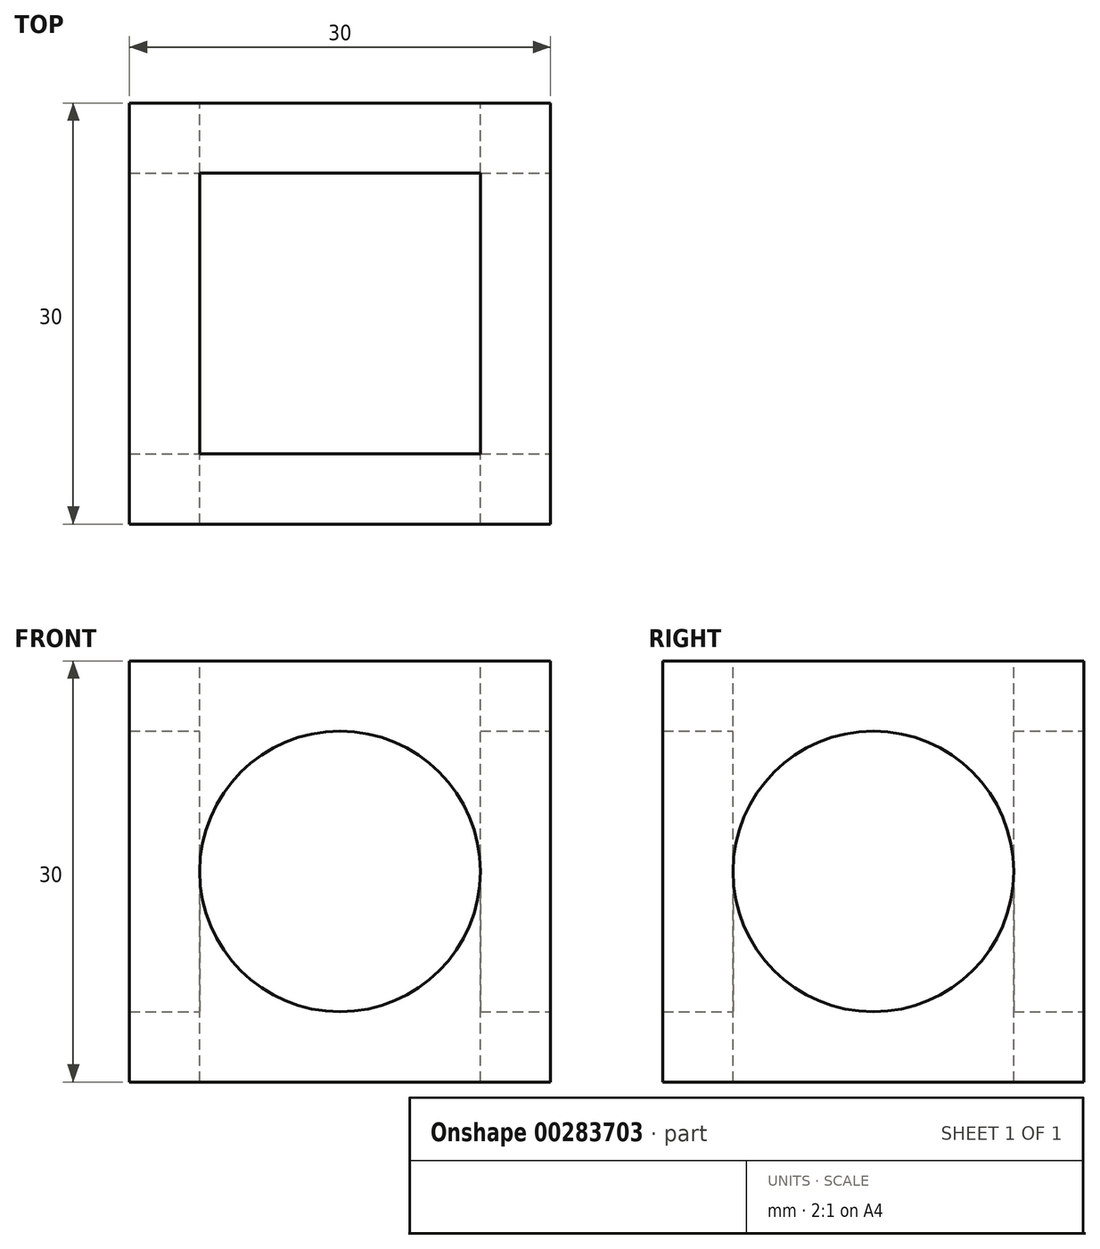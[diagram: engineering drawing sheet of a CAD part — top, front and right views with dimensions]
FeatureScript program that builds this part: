
annotation { "Feature Type Name" : "Feature", "Feature Type Description" : "" }
export const myFeature = defineFeature(function(context is Context, id is Id, definition is map)
    precondition{}
    {
        {
            var Q0;
            Q0=qCreatedBy(makeId("Top.planeOp"),FACE);
            var sketch = newSketch(context, id + "F0", { "sketchPlane" : qUnion([Q0])});
            skLineSegment(sketch, "E0.bottom", {"start": v(15, 15) * mm, "end": v(-15, 15) * mm});
            skLineSegment(sketch, "E0.top", {"start": v(15, -15) * mm, "end": v(-15, -15) * mm});
            skLineSegment(sketch, "E0.left", {"start": v(15, 15) * mm, "end": v(15, -15) * mm});
            skLineSegment(sketch, "E0.right", {"start": v(-15, 15) * mm, "end": v(-15, -15) * mm});
            skPoint(sketch, "E0.middle", {"position": v(0, 0) * mm});
            skSolve(sketch);
        }
        {
            var Q0;
            Q0 = qSketchRegion(id + "F0", true);
            extrude(context, id + "F1", {"entities" : qUnion([Q0]), "endBound" : BoundingType.SYMMETRIC, "depth" : 30 * mm});
        }
        {
            var Q0;
            Q0=makeQuery(id+"F1.opExtrude","CAP_FACE",FACE,{"disambiguationData":[OSD([sQuery(id+"F0.wireOp",EDGE,"E0.bottom"),sQuery(id+"F0.wireOp",EDGE,"E0.top"),sQuery(id+"F0.wireOp",EDGE,"E0.left"),sQuery(id+"F0.wireOp",EDGE,"E0.right")])],"isStart":false});
            var sketch = newSketch(context, id + "F2", { "sketchPlane" : qUnion([Q0])});
            skLineSegment(sketch, "E1.bottom", {"start": v(10, 10) * mm, "end": v(-10, 10) * mm});
            skLineSegment(sketch, "E1.top", {"start": v(10, -10) * mm, "end": v(-10, -10) * mm});
            skLineSegment(sketch, "E1.left", {"start": v(10, 10) * mm, "end": v(10, -10) * mm});
            skLineSegment(sketch, "E1.right", {"start": v(-10, 10) * mm, "end": v(-10, -10) * mm});
            skPoint(sketch, "E1.middle", {"position": v(0, 0) * mm});
            skSolve(sketch);
        }
        {
            var Q0;
            Q0 = qSketchRegion(id + "F2", true);
            extrude(context, id + "F3", {"entities" : qUnion([Q0]), "operationType" : NewBodyOperationType.REMOVE, "oppositeDirection" : true, "depth" : 30 * mm});
        }
        {
            var Q0;
            Q0=makeQuery(id+"F1.opExtrude","SWEPT_FACE",FACE,{"disambiguationData":[OSD([sQuery(id+"F0.wireOp",EDGE,"E0.left")])]});
            var sketch = newSketch(context, id + "F4", { "sketchPlane" : qUnion([Q0])});
            skCircle(sketch, "E2", {"center": v(0, 0) * mm, "radius": 10 * mm});
            skSolve(sketch);
        }
        {
            var Q0;
            Q0 = qSketchRegion(id + "F4", true);
            extrude(context, id + "F5", {"entities" : qUnion([Q0]), "operationType" : NewBodyOperationType.REMOVE, "oppositeDirection" : true, "depth" : 30 * mm});
        }
        {
            var Q0;
            Q0=makeQuery(id+"F1.opExtrude","SWEPT_FACE",FACE,{"disambiguationData":[OSD([sQuery(id+"F0.wireOp",EDGE,"E0.bottom")])]});
            var sketch = newSketch(context, id + "F6", { "sketchPlane" : qUnion([Q0])});
            skCircle(sketch, "E3", {"center": v(0, 0) * mm, "radius": 10 * mm});
            skSolve(sketch);
        }
        {
            var Q0;
            Q0 = qSketchRegion(id + "F6", true);
            extrude(context, id + "F7", {"entities" : qUnion([Q0]), "operationType" : NewBodyOperationType.REMOVE, "oppositeDirection" : true, "depth" : 30 * mm});
        }
    });
